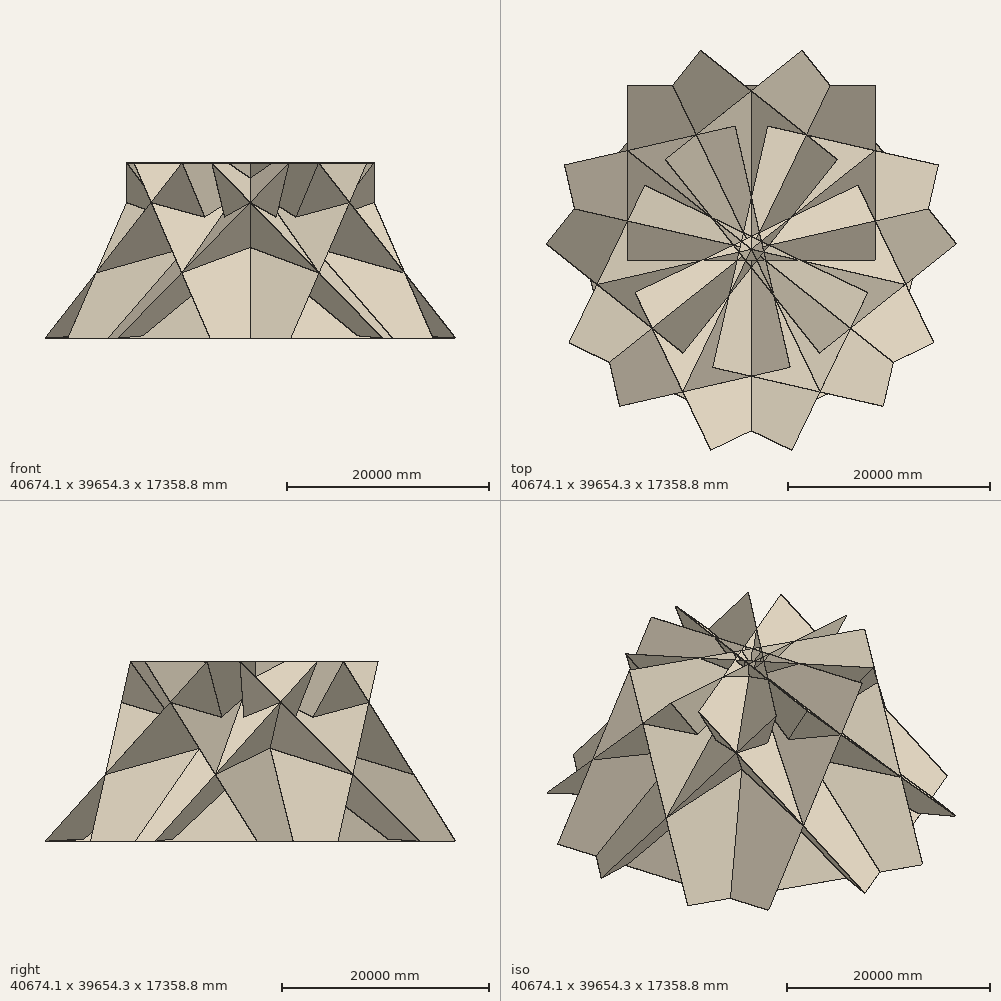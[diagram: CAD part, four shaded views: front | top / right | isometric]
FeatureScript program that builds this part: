
annotation { "Feature Type Name" : "Feature", "Feature Type Description" : "" }
export const myFeature = defineFeature(function(context is Context, id is Id, definition is map)
    precondition{}
    {
        {
            var Q0;
            Q0=qCreatedBy(makeId("Top.planeOp"),FACE);
            var sketch = newSketch(context, id + "F0", { "sketchPlane" : qUnion([Q0])});
            skCircle(sketch, "E0", {"center": v(0, 0) * mm, "radius": 3657.6 * mm});
            skLineSegment(sketch, "E1", {"start": v(0, 0) * mm, "end": v(0, -3657.6) * mm});
            skSolve(sketch);
        }
        {
            var Q0;
            Q0=qCreatedBy(makeId("Right.planeOp"),FACE);
            var sketch = newSketch(context, id + "F1", { "sketchPlane" : qUnion([Q0])});
            skLineSegment(sketch, "E2", {"start": v(-3657.6, 0) * mm, "end": v(-1812.88, 1844.72) * mm, "construction": true});
            skLineSegment(sketch, "E3", {"start": v(0, 0) * mm, "end": v(0, 3105.65) * mm, "construction": true});
            skSolve(sketch);
        }
        {
            var Q0;
            Q0=sQuery(id+"F0.wireOp",VERTEX,"E1.end");
            var Q1;
            Q1=sQuery(id+"F1.wireOp",EDGE,"E2");
            cPlane(context, id + "F2", {"entities" : qUnion([Q0, Q1]), "cplaneType" : CPlaneType.LINE_POINT, "offset" : 25 * mm, "width" : 150 * mm, "height" : 150 * mm});
        }
        {
            var Q0;
            Q0=qCreatedBy(id+"F2.planeOp",FACE);
            var sketch = newSketch(context, id + "F3", { "sketchPlane" : qUnion([Q0])});
            skLineSegment(sketch, "E4.bottom", {"start": v(3.2, -2583.91) * mm, "end": v(-3.2, -2583.91) * mm});
            skLineSegment(sketch, "E4.top", {"start": v(3.2, -2588.71) * mm, "end": v(-3.2, -2588.71) * mm});
            skLineSegment(sketch, "E4.left", {"start": v(3.2, -2583.91) * mm, "end": v(3.2, -2588.71) * mm});
            skLineSegment(sketch, "E4.right", {"start": v(-3.2, -2583.91) * mm, "end": v(-3.2, -2588.71) * mm});
            skPoint(sketch, "E4.middle", {"position": v(0, -2586.31) * mm});
            skSolve(sketch);
        }
        {
            var Q0;
            Q0 = qSketchRegion(id + "F0", true);
            var Q1;
            Q1=sQuery(id+"F0.wireOp",EDGE,"E0");
            extrude(context, id + "F4", {"entities" : qUnion([Q0]), "surfaceEntities" : qUnion([Q1]), "depth" : 6096 * mm});
        }
        {
            var Q0;
            Q0=makeQuery(id+"F3.imprint","IMPRINT",FACE,{"disambiguationData":[TD([[makeQuery(id+"F3.imprint","IMPRINT",EDGE,{"derivedFrom":sQuery(id+"F3.wireOp",EDGE,"E4.bottom")}),1.0]])]});
            extrude(context, id + "F5", {"entities" : qUnion([Q0]), "depth" : 10668 * mm, "hasDraft" : true, "draftAngle" : 49 * degree});
        }
        {
            var Q0;
            Q0=makeQuery(id+"F5.opExtrude","SWEPT_BODY",BODY,{"disambiguationData":[OSD([sQuery(id+"F3.wireOp",EDGE,"E4.bottom"),sQuery(id+"F3.wireOp",EDGE,"E4.top"),sQuery(id+"F3.wireOp",EDGE,"E4.left"),sQuery(id+"F3.wireOp",EDGE,"E4.right")])]});
            var Q1;
            Q1=sQuery(id+"F1.wireOp",EDGE,"E3");
            circularPattern(context, id + "F6", {"entities" : qUnion([Q0]), "axis" : qUnion([Q1]), "angle" : 360 * degree, "instanceCount" : 7, "equalSpace" : true});
        }
        {
            var Q0;
            Q0=makeQuery(id+"F5.opExtrude","SWEPT_BODY",BODY,{"disambiguationData":[OSD([sQuery(id+"F3.wireOp",EDGE,"E4.bottom"),sQuery(id+"F3.wireOp",EDGE,"E4.top"),sQuery(id+"F3.wireOp",EDGE,"E4.left"),sQuery(id+"F3.wireOp",EDGE,"E4.right")])]});
            var Q1;
            Q1=makeQuery(id+"F6.opPattern","COPY",BODY,{"derivedFrom":makeQuery(id+"F5.opExtrude","SWEPT_BODY",BODY,{"disambiguationData":[OSD([sQuery(id+"F3.wireOp",EDGE,"E4.bottom"),sQuery(id+"F3.wireOp",EDGE,"E4.top"),sQuery(id+"F3.wireOp",EDGE,"E4.left"),sQuery(id+"F3.wireOp",EDGE,"E4.right")])]}),"instanceName":"1"});
            var Q2;
            Q2=makeQuery(id+"F4.opExtrude","SWEPT_BODY",BODY,{"disambiguationData":[OSD([sQuery(id+"F0.wireOp",EDGE,"E0")])]});
            booleanBodies(context, id + "F7", {"operationType" : BooleanOperationType.INTERSECTION, "tools" : qUnion([Q0, Q1, Q2]), "keepTools" : true});
        }
        {
            var Q0;
            Q0=makeQuery(id+"F6.opPattern","COPY",BODY,{"derivedFrom":makeQuery(id+"F5.opExtrude","SWEPT_BODY",BODY,{"disambiguationData":[OSD([sQuery(id+"F3.wireOp",EDGE,"E4.bottom"),sQuery(id+"F3.wireOp",EDGE,"E4.top"),sQuery(id+"F3.wireOp",EDGE,"E4.left"),sQuery(id+"F3.wireOp",EDGE,"E4.right")])]}),"instanceName":"4"});
            var Q1;
            Q1=makeQuery(id+"F6.opPattern","COPY",BODY,{"derivedFrom":makeQuery(id+"F5.opExtrude","SWEPT_BODY",BODY,{"disambiguationData":[OSD([sQuery(id+"F3.wireOp",EDGE,"E4.bottom"),sQuery(id+"F3.wireOp",EDGE,"E4.top"),sQuery(id+"F3.wireOp",EDGE,"E4.left"),sQuery(id+"F3.wireOp",EDGE,"E4.right")])]}),"instanceName":"2"});
            var Q2;
            Q2=makeQuery(id+"F4.opExtrude","SWEPT_BODY",BODY,{"disambiguationData":[OSD([sQuery(id+"F0.wireOp",EDGE,"E0")])]});
            booleanBodies(context, id + "F8", {"operationType" : BooleanOperationType.INTERSECTION, "tools" : qUnion([Q0, Q1, Q2]), "keepTools" : true});
        }
    });
